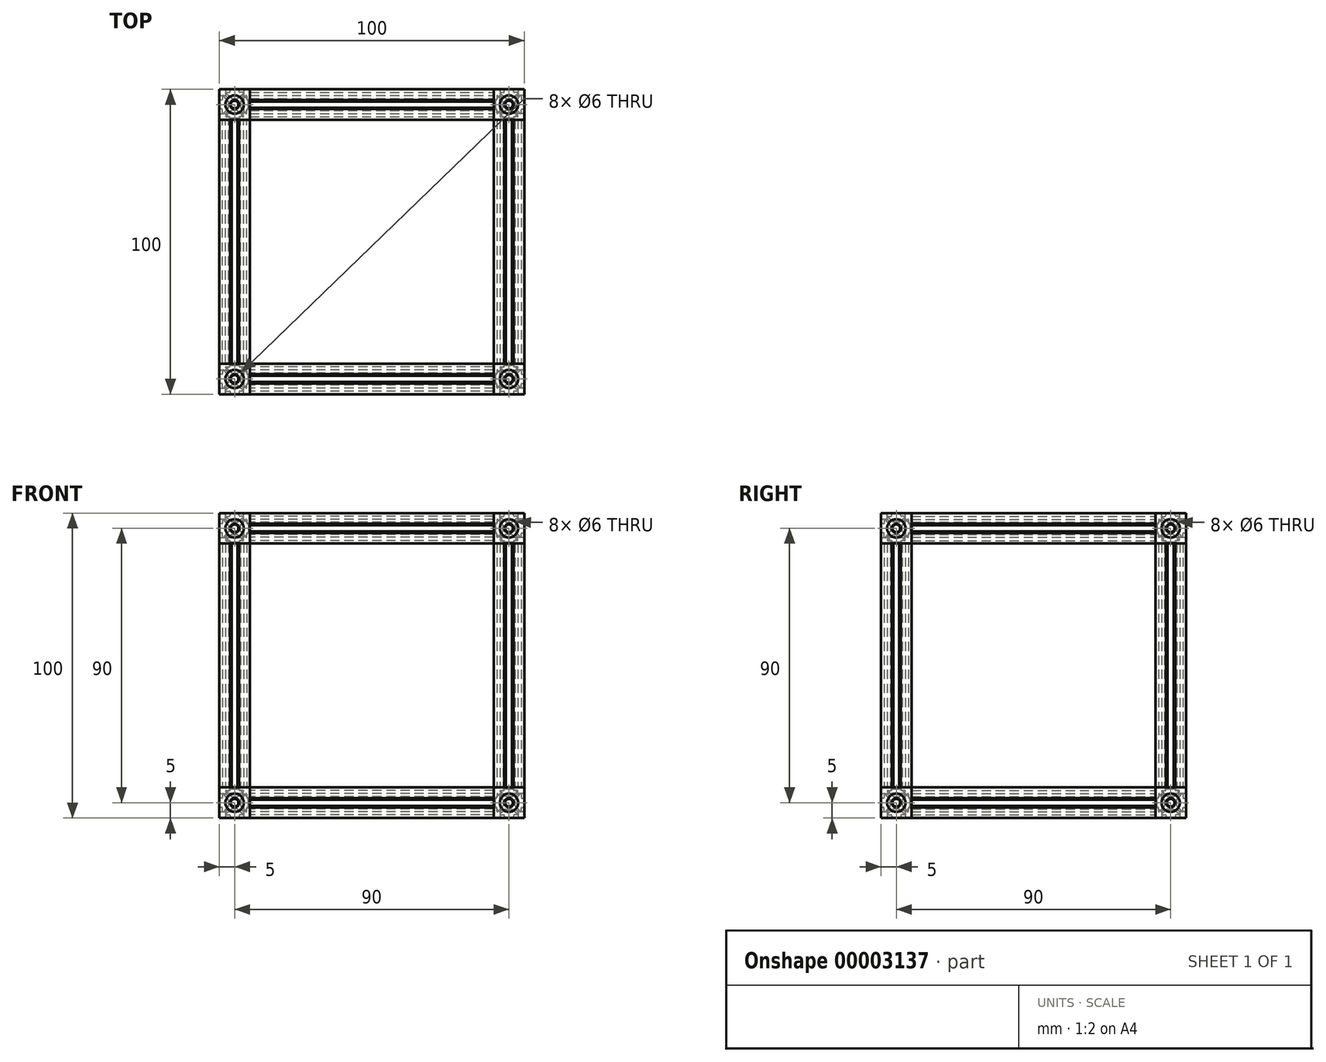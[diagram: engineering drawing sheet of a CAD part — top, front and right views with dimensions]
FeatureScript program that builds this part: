
annotation { "Feature Type Name" : "Feature", "Feature Type Description" : "" }
export const myFeature = defineFeature(function(context is Context, id is Id, definition is map)
    precondition{}
    {
        {
            var Q0;
            Q0=qCreatedBy(makeId("Front.planeOp"),FACE);
            var sketch = newSketch(context, id + "F0", { "sketchPlane" : qUnion([Q0])});
            skLineSegment(sketch, "E0", {"start": v(0, 0) * mm, "end": v(0, 5) * mm, "construction": true});
            skLineSegment(sketch, "E1", {"start": v(0, 0) * mm, "end": v(5, 5) * mm, "construction": true});
            skLineSegment(sketch, "E2", {"start": v(5, 5) * mm, "end": v(0, 5) * mm, "construction": true});
            skLineSegment(sketch, "E3", {"start": v(0, 2) * mm, "end": v(1, 2) * mm});
            skLineSegment(sketch, "E4", {"start": v(1, 2) * mm, "end": v(2.9, 3.65) * mm});
            skLineSegment(sketch, "E5", {"start": v(2.76, 4) * mm, "end": v(1.7, 4) * mm});
            skLineSegment(sketch, "E6", {"start": v(1.5, 4.2) * mm, "end": v(1.5, 4.8) * mm});
            skLineSegment(sketch, "E7", {"start": v(1.7, 5) * mm, "end": v(4.8, 5) * mm});
            skLineSegment(sketch, "E8.0.MirrorCS", {"start": v(5, 1.7) * mm, "end": v(5, 4.8) * mm});
            skLineSegment(sketch, "E8.1.MirrorCS", {"start": v(4.2, 1.5) * mm, "end": v(4.8, 1.5) * mm});
            skLineSegment(sketch, "E8.2.MirrorCS", {"start": v(4, 2.76) * mm, "end": v(4, 1.7) * mm});
            skLineSegment(sketch, "E8.3.MirrorCS", {"start": v(2, 0) * mm, "end": v(2, 1) * mm});
            skLineSegment(sketch, "E8.4.MirrorCS", {"start": v(2, 1) * mm, "end": v(3.65, 2.9) * mm});
            skLineSegment(sketch, "E9.0.MirrorCS", {"start": v(-2, 0) * mm, "end": v(-2, 1) * mm});
            skLineSegment(sketch, "E9.1.MirrorCS", {"start": v(-2, 1) * mm, "end": v(-3.65, 2.9) * mm});
            skLineSegment(sketch, "E9.2.MirrorCS", {"start": v(-4, 2.76) * mm, "end": v(-4, 1.7) * mm});
            skLineSegment(sketch, "E9.3.MirrorCS", {"start": v(-4.2, 1.5) * mm, "end": v(-4.8, 1.5) * mm});
            skLineSegment(sketch, "E9.4.MirrorCS", {"start": v(-5, 1.7) * mm, "end": v(-5, 4.8) * mm});
            skLineSegment(sketch, "E9.5.MirrorCS", {"start": v(-1.7, 5) * mm, "end": v(-4.8, 5) * mm});
            skLineSegment(sketch, "E9.6.MirrorCS", {"start": v(-1.5, 4.2) * mm, "end": v(-1.5, 4.8) * mm});
            skLineSegment(sketch, "E9.7.MirrorCS", {"start": v(-2.76, 4) * mm, "end": v(-1.7, 4) * mm});
            skLineSegment(sketch, "E9.8.MirrorCS", {"start": v(0, 2) * mm, "end": v(-1, 2) * mm});
            skLineSegment(sketch, "E9.9.MirrorCS", {"start": v(-1, 2) * mm, "end": v(-2.9, 3.65) * mm});
            skLineSegment(sketch, "E10.0.MirrorCS", {"start": v(0, 0) * mm, "end": v(5, 0) * mm, "construction": true});
            skLineSegment(sketch, "E11.0.MirrorCS", {"start": v(2, 0) * mm, "end": v(2, -1) * mm});
            skLineSegment(sketch, "E12.0.MirrorCS", {"start": v(2, -1) * mm, "end": v(3.65, -2.9) * mm});
            skLineSegment(sketch, "E13.0.MirrorCS", {"start": v(4.2, -1.5) * mm, "end": v(4.8, -1.5) * mm});
            skLineSegment(sketch, "E14.0.MirrorCS", {"start": v(5, -1.7) * mm, "end": v(5, -4.8) * mm});
            skLineSegment(sketch, "E15.0.MirrorCS", {"start": v(1.7, -5) * mm, "end": v(4.8, -5) * mm});
            skLineSegment(sketch, "E16.0.MirrorCS", {"start": v(1.5, -4.2) * mm, "end": v(1.5, -4.8) * mm});
            skLineSegment(sketch, "E17.0.MirrorCS", {"start": v(2.76, -4) * mm, "end": v(1.7, -4) * mm});
            skLineSegment(sketch, "E18.0.MirrorCS", {"start": v(1, -2) * mm, "end": v(2.9, -3.65) * mm});
            skLineSegment(sketch, "E19.0.MirrorCS", {"start": v(0, -2) * mm, "end": v(1, -2) * mm});
            skLineSegment(sketch, "E20.0.MirrorCS", {"start": v(0, -2) * mm, "end": v(-1, -2) * mm});
            skLineSegment(sketch, "E21.0.MirrorCS", {"start": v(-1, -2) * mm, "end": v(-2.9, -3.65) * mm});
            skLineSegment(sketch, "E22.0.MirrorCS", {"start": v(-2.76, -4) * mm, "end": v(-1.7, -4) * mm});
            skLineSegment(sketch, "E23.0.MirrorCS", {"start": v(-1.5, -4.2) * mm, "end": v(-1.5, -4.8) * mm});
            skLineSegment(sketch, "E24.0.MirrorCS", {"start": v(-1.7, -5) * mm, "end": v(-4.8, -5) * mm});
            skLineSegment(sketch, "E25.0.MirrorCS", {"start": v(-5, -1.7) * mm, "end": v(-5, -4.8) * mm});
            skLineSegment(sketch, "E26.0.MirrorCS", {"start": v(-4.2, -1.5) * mm, "end": v(-4.8, -1.5) * mm});
            skLineSegment(sketch, "E27.0.MirrorCS", {"start": v(-4, -2.76) * mm, "end": v(-4, -1.7) * mm});
            skLineSegment(sketch, "E28.0.MirrorCS", {"start": v(-2, -1) * mm, "end": v(-3.65, -2.9) * mm});
            skLineSegment(sketch, "E29.0.MirrorCS", {"start": v(-2, 0) * mm, "end": v(-2, -1) * mm});
            skLineSegment(sketch, "E30.0.MirrorCS", {"start": v(4, -2.76) * mm, "end": v(4, -1.7) * mm});
            skCircle(sketch, "E31", {"center": v(0, 0) * mm, "radius": 1.25 * mm});
            skPoint(sketch, "E32.visualSharp", {"position": v(-4, 3.3) * mm});
            skArc(sketch, "E32.filletArc", {"start": v(-3.65, 2.9) * mm, "mid": v(-3.87, 2.95) * mm, "end": v(-4, 2.76) * mm});
            skPoint(sketch, "E33.visualSharp", {"position": v(-5, 1.5) * mm});
            skArc(sketch, "E33.filletArc", {"start": v(-5, 1.7) * mm, "mid": v(-4.94, 1.56) * mm, "end": v(-4.8, 1.5) * mm});
            skPoint(sketch, "E34.visualSharp", {"position": v(-4, 1.5) * mm});
            skArc(sketch, "E34.filletArc", {"start": v(-4.2, 1.5) * mm, "mid": v(-4.06, 1.56) * mm, "end": v(-4, 1.7) * mm});
            skPoint(sketch, "E35.visualSharp", {"position": v(-5, 5) * mm});
            skArc(sketch, "E35.filletArc", {"start": v(-4.8, 5) * mm, "mid": v(-4.94, 4.94) * mm, "end": v(-5, 4.8) * mm});
            skPoint(sketch, "E36.visualSharp", {"position": v(-1.5, 5) * mm});
            skArc(sketch, "E36.filletArc", {"start": v(-1.5, 4.8) * mm, "mid": v(-1.56, 4.94) * mm, "end": v(-1.7, 5) * mm});
            skPoint(sketch, "E37.visualSharp", {"position": v(-1.5, 4) * mm});
            skArc(sketch, "E37.filletArc", {"start": v(-1.7, 4) * mm, "mid": v(-1.56, 4.06) * mm, "end": v(-1.5, 4.2) * mm});
            skPoint(sketch, "E38.visualSharp", {"position": v(-3.3, 4) * mm});
            skArc(sketch, "E38.filletArc", {"start": v(-2.76, 4) * mm, "mid": v(-2.95, 3.87) * mm, "end": v(-2.9, 3.65) * mm});
            skPoint(sketch, "E39.visualSharp", {"position": v(3.3, 4) * mm});
            skArc(sketch, "E39.filletArc", {"start": v(2.9, 3.65) * mm, "mid": v(2.95, 3.87) * mm, "end": v(2.76, 4) * mm});
            skPoint(sketch, "E40.visualSharp", {"position": v(1.5, 4) * mm});
            skArc(sketch, "E40.filletArc", {"start": v(1.5, 4.2) * mm, "mid": v(1.56, 4.06) * mm, "end": v(1.7, 4) * mm});
            skPoint(sketch, "E41.visualSharp", {"position": v(1.5, 5) * mm});
            skArc(sketch, "E41.filletArc", {"start": v(1.7, 5) * mm, "mid": v(1.56, 4.94) * mm, "end": v(1.5, 4.8) * mm});
            skPoint(sketch, "E42.visualSharp", {"position": v(5, 5) * mm});
            skArc(sketch, "E42.filletArc", {"start": v(5, 4.8) * mm, "mid": v(4.94, 4.94) * mm, "end": v(4.8, 5) * mm});
            skPoint(sketch, "E43.visualSharp", {"position": v(5, 1.5) * mm});
            skArc(sketch, "E43.filletArc", {"start": v(4.8, 1.5) * mm, "mid": v(4.94, 1.56) * mm, "end": v(5, 1.7) * mm});
            skPoint(sketch, "E44.visualSharp", {"position": v(4, 1.5) * mm});
            skArc(sketch, "E44.filletArc", {"start": v(4, 1.7) * mm, "mid": v(4.06, 1.56) * mm, "end": v(4.2, 1.5) * mm});
            skPoint(sketch, "E45.visualSharp", {"position": v(4, 3.3) * mm});
            skArc(sketch, "E45.filletArc", {"start": v(4, 2.76) * mm, "mid": v(3.87, 2.95) * mm, "end": v(3.65, 2.9) * mm});
            skPoint(sketch, "E46.visualSharp", {"position": v(4, -1.5) * mm});
            skArc(sketch, "E46.filletArc", {"start": v(4.2, -1.5) * mm, "mid": v(4.06, -1.56) * mm, "end": v(4, -1.7) * mm});
            skPoint(sketch, "E47.visualSharp", {"position": v(5, -1.5) * mm});
            skArc(sketch, "E47.filletArc", {"start": v(5, -1.7) * mm, "mid": v(4.94, -1.56) * mm, "end": v(4.8, -1.5) * mm});
            skPoint(sketch, "E48.visualSharp", {"position": v(4, -3.3) * mm});
            skArc(sketch, "E48.filletArc", {"start": v(3.65, -2.9) * mm, "mid": v(3.87, -2.95) * mm, "end": v(4, -2.76) * mm});
            skPoint(sketch, "E49.visualSharp", {"position": v(3.3, -4) * mm});
            skArc(sketch, "E49.filletArc", {"start": v(2.76, -4) * mm, "mid": v(2.95, -3.87) * mm, "end": v(2.9, -3.65) * mm});
            skPoint(sketch, "E50.visualSharp", {"position": v(5, -5) * mm});
            skArc(sketch, "E50.filletArc", {"start": v(4.8, -5) * mm, "mid": v(4.94, -4.94) * mm, "end": v(5, -4.8) * mm});
            skPoint(sketch, "E51.visualSharp", {"position": v(1.5, -5) * mm});
            skArc(sketch, "E51.filletArc", {"start": v(1.5, -4.8) * mm, "mid": v(1.56, -4.94) * mm, "end": v(1.7, -5) * mm});
            skPoint(sketch, "E52.visualSharp", {"position": v(1.5, -4) * mm});
            skArc(sketch, "E52.filletArc", {"start": v(1.7, -4) * mm, "mid": v(1.56, -4.06) * mm, "end": v(1.5, -4.2) * mm});
            skPoint(sketch, "E53.visualSharp", {"position": v(-1.5, -4) * mm});
            skArc(sketch, "E53.filletArc", {"start": v(-1.5, -4.2) * mm, "mid": v(-1.56, -4.06) * mm, "end": v(-1.7, -4) * mm});
            skPoint(sketch, "E54.visualSharp", {"position": v(-1.5, -5) * mm});
            skArc(sketch, "E54.filletArc", {"start": v(-1.7, -5) * mm, "mid": v(-1.56, -4.94) * mm, "end": v(-1.5, -4.8) * mm});
            skPoint(sketch, "E55.visualSharp", {"position": v(-3.3, -4) * mm});
            skArc(sketch, "E55.filletArc", {"start": v(-2.9, -3.65) * mm, "mid": v(-2.95, -3.87) * mm, "end": v(-2.76, -4) * mm});
            skPoint(sketch, "E56.visualSharp", {"position": v(-5, -5) * mm});
            skArc(sketch, "E56.filletArc", {"start": v(-5, -4.8) * mm, "mid": v(-4.94, -4.94) * mm, "end": v(-4.8, -5) * mm});
            skPoint(sketch, "E57.visualSharp", {"position": v(-4, -3.3) * mm});
            skArc(sketch, "E57.filletArc", {"start": v(-4, -2.76) * mm, "mid": v(-3.87, -2.95) * mm, "end": v(-3.65, -2.9) * mm});
            skPoint(sketch, "E58.visualSharp", {"position": v(-4, -1.5) * mm});
            skArc(sketch, "E58.filletArc", {"start": v(-4, -1.7) * mm, "mid": v(-4.06, -1.56) * mm, "end": v(-4.2, -1.5) * mm});
            skPoint(sketch, "E59.visualSharp", {"position": v(-5, -1.5) * mm});
            skArc(sketch, "E59.filletArc", {"start": v(-4.8, -1.5) * mm, "mid": v(-4.94, -1.56) * mm, "end": v(-5, -1.7) * mm});
            skSolve(sketch);
        }
        {
            var Q0;
            Q0=makeQuery(id+"F0.imprint","IMPRINT",FACE,{"disambiguationData":[TD([[makeQuery(id+"F0.imprint","IMPRINT",EDGE,{"derivedFrom":sQuery(id+"F0.wireOp",EDGE,"E3")}),-1.0]])]});
            extrude(context, id + "F1", {"entities" : qUnion([Q0]), "depth" : 80 * mm});
        }
        {
            var Q0;
            Q0=qCreatedBy(makeId("Front.planeOp"),FACE);
            var sketch = newSketch(context, id + "F2", { "sketchPlane" : qUnion([Q0])});
            skLineSegment(sketch, "E60.bottom", {"start": v(5, 5) * mm, "end": v(-5, 5) * mm});
            skLineSegment(sketch, "E60.left", {"start": v(5, 5) * mm, "end": v(5, -5) * mm});
            skLineSegment(sketch, "E61", {"start": v(5, -5) * mm, "end": v(-5, -5) * mm});
            skLineSegment(sketch, "E62", {"start": v(-5, -5) * mm, "end": v(-5, 5) * mm});
            skSolve(sketch);
        }
        {
            var Q0;
            Q0=makeQuery(id+"F2.imprint","IMPRINT",FACE,{"disambiguationData":[TD([[makeQuery(id+"F2.imprint","IMPRINT",EDGE,{"derivedFrom":sQuery(id+"F2.wireOp",EDGE,"E60.bottom")}),1.0]])]});
            extrude(context, id + "F3", {"entities" : qUnion([Q0]), "oppositeDirection" : true, "depth" : 10 * mm});
        }
        {
            var Q0;
            Q0=qCreatedBy(makeId("Top.planeOp"),FACE);
            var sketch = newSketch(context, id + "F4", { "sketchPlane" : qUnion([Q0])});
            skLineSegment(sketch, "E63", {"start": v(0, 0) * mm, "end": v(0, 10) * mm, "construction": true});
            skLineSegment(sketch, "E64", {"start": v(1.5, 0) * mm, "end": v(1.5, 0.5) * mm});
            skLineSegment(sketch, "E65", {"start": v(1.5, 0.5) * mm, "end": v(3, 2) * mm});
            skLineSegment(sketch, "E66", {"start": v(3, 2) * mm, "end": v(3, 10) * mm});
            skLineSegment(sketch, "E67", {"start": v(0, 10) * mm, "end": v(3, 10) * mm});
            skLineSegment(sketch, "E68", {"start": v(0, 0) * mm, "end": v(1.5, 0) * mm});
            skLineSegment(sketch, "E69", {"start": v(0, 10) * mm, "end": v(0, 0) * mm});
            skSolve(sketch);
        }
        {
            var Q0;
            Q0=makeQuery(id+"F4.imprint","IMPRINT",FACE,{"disambiguationData":[TD([[makeQuery(id+"F4.imprint","IMPRINT",EDGE,{"derivedFrom":sQuery(id+"F4.wireOp",EDGE,"E64")}),1.0]])]});
            var Q1;
            Q1=sQuery(id+"F4.wireOp",EDGE,"E69");
            revolve(context, id + "F5", {"operationType" : NewBodyOperationType.REMOVE, "entities" : qUnion([Q0]), "axis" : qUnion([Q1]), "revolveType" : RevolveType.FULL, "oppositeDirection" : true});
        }
        {
            var Q0;
            Q0=qCreatedBy(makeId("Top.planeOp"),FACE);
            var sketch = newSketch(context, id + "F6", { "sketchPlane" : qUnion([Q0])});
            skLineSegment(sketch, "E70", {"start": v(-5, 5) * mm, "end": v(5, 5) * mm, "construction": true});
            skLineSegment(sketch, "E71", {"start": v(-5, 5) * mm, "end": v(5, 5) * mm});
            skLineSegment(sketch, "E72", {"start": v(5, 5) * mm, "end": v(5, 6.5) * mm});
            skLineSegment(sketch, "E73", {"start": v(5, 6.5) * mm, "end": v(4.5, 6.5) * mm});
            skLineSegment(sketch, "E74", {"start": v(4.5, 6.5) * mm, "end": v(3, 8) * mm});
            skLineSegment(sketch, "E75", {"start": v(3, 8) * mm, "end": v(-5, 8) * mm});
            skLineSegment(sketch, "E76", {"start": v(-5, 8) * mm, "end": v(-5, 5) * mm});
            skSolve(sketch);
        }
        {
            var Q0;
            Q0=makeQuery(id+"F6.imprint","IMPRINT",FACE,{"disambiguationData":[TD([[makeQuery(id+"F6.imprint","IMPRINT",EDGE,{"derivedFrom":sQuery(id+"F6.wireOp",EDGE,"E71")}),1.0]])]});
            var Q1;
            Q1=sQuery(id+"F6.wireOp",EDGE,"E71");
            revolve(context, id + "F7", {"operationType" : NewBodyOperationType.REMOVE, "entities" : qUnion([Q0]), "axis" : qUnion([Q1]), "revolveType" : RevolveType.FULL, "oppositeDirection" : true});
        }
        {
            var Q0;
            Q0=qCreatedBy(makeId("Right.planeOp"),FACE);
            var sketch = newSketch(context, id + "F8", { "sketchPlane" : qUnion([Q0])});
            skLineSegment(sketch, "E77", {"start": v(5, 5) * mm, "end": v(5, -5) * mm, "construction": true});
            skLineSegment(sketch, "E78", {"start": v(5, 5) * mm, "end": v(6.5, 5) * mm});
            skLineSegment(sketch, "E79", {"start": v(6.5, 5) * mm, "end": v(6.5, 4.5) * mm});
            skLineSegment(sketch, "E80", {"start": v(6.5, 4.5) * mm, "end": v(8, 3) * mm});
            skLineSegment(sketch, "E81", {"start": v(8, 3) * mm, "end": v(8, -5) * mm});
            skLineSegment(sketch, "E82", {"start": v(8, -5) * mm, "end": v(5, -5) * mm});
            skLineSegment(sketch, "E83", {"start": v(5, -5) * mm, "end": v(5, 5) * mm});
            skSolve(sketch);
        }
        {
            var Q0;
            Q0=makeQuery(id+"F8.imprint","IMPRINT",FACE,{"disambiguationData":[TD([[makeQuery(id+"F8.imprint","IMPRINT",EDGE,{"derivedFrom":sQuery(id+"F8.wireOp",EDGE,"E78")}),-1.0]])]});
            var Q1;
            Q1=sQuery(id+"F8.wireOp",EDGE,"E83");
            revolve(context, id + "F9", {"operationType" : NewBodyOperationType.REMOVE, "entities" : qUnion([Q0]), "axis" : qUnion([Q1]), "revolveType" : RevolveType.FULL});
        }
        {
            var Q0;
            Q0=makeQuery(id+"F1.opExtrude","SWEPT_BODY",BODY,{"disambiguationData":[OSD([sQuery(id+"F0.wireOp",EDGE,"E3"),sQuery(id+"F0.wireOp",EDGE,"E4"),sQuery(id+"F0.wireOp",EDGE,"E5"),sQuery(id+"F0.wireOp",EDGE,"E6"),sQuery(id+"F0.wireOp",EDGE,"E7"),sQuery(id+"F0.wireOp",EDGE,"E8.0.MirrorCS"),sQuery(id+"F0.wireOp",EDGE,"E8.1.MirrorCS"),sQuery(id+"F0.wireOp",EDGE,"E8.2.MirrorCS"),sQuery(id+"F0.wireOp",EDGE,"E8.4.MirrorCS"),sQuery(id+"F0.wireOp",EDGE,"E9.0.MirrorCS"),sQuery(id+"F0.wireOp",EDGE,"E9.1.MirrorCS"),sQuery(id+"F0.wireOp",EDGE,"E9.2.MirrorCS"),sQuery(id+"F0.wireOp",EDGE,"E9.3.MirrorCS"),sQuery(id+"F0.wireOp",EDGE,"E9.4.MirrorCS"),sQuery(id+"F0.wireOp",EDGE,"E9.5.MirrorCS"),sQuery(id+"F0.wireOp",EDGE,"E9.6.MirrorCS"),sQuery(id+"F0.wireOp",EDGE,"E9.7.MirrorCS"),sQuery(id+"F0.wireOp",EDGE,"E9.9.MirrorCS"),sQuery(id+"F0.wireOp",EDGE,"E11.0.MirrorCS"),sQuery(id+"F0.wireOp",EDGE,"E12.0.MirrorCS"),sQuery(id+"F0.wireOp",EDGE,"E13.0.MirrorCS"),sQuery(id+"F0.wireOp",EDGE,"E14.0.MirrorCS"),sQuery(id+"F0.wireOp",EDGE,"E15.0.MirrorCS"),sQuery(id+"F0.wireOp",EDGE,"E16.0.MirrorCS"),sQuery(id+"F0.wireOp",EDGE,"E17.0.MirrorCS"),sQuery(id+"F0.wireOp",EDGE,"E18.0.MirrorCS"),sQuery(id+"F0.wireOp",EDGE,"E20.0.MirrorCS"),sQuery(id+"F0.wireOp",EDGE,"E21.0.MirrorCS"),sQuery(id+"F0.wireOp",EDGE,"E22.0.MirrorCS"),sQuery(id+"F0.wireOp",EDGE,"E23.0.MirrorCS"),sQuery(id+"F0.wireOp",EDGE,"E24.0.MirrorCS"),sQuery(id+"F0.wireOp",EDGE,"E25.0.MirrorCS"),sQuery(id+"F0.wireOp",EDGE,"E26.0.MirrorCS"),sQuery(id+"F0.wireOp",EDGE,"E27.0.MirrorCS"),sQuery(id+"F0.wireOp",EDGE,"E28.0.MirrorCS"),sQuery(id+"F0.wireOp",EDGE,"E30.0.MirrorCS"),sQuery(id+"F0.wireOp",EDGE,"E31"),sQuery(id+"F0.wireOp",EDGE,"E32.filletArc"),sQuery(id+"F0.wireOp",EDGE,"E33.filletArc"),sQuery(id+"F0.wireOp",EDGE,"E34.filletArc"),sQuery(id+"F0.wireOp",EDGE,"E35.filletArc"),sQuery(id+"F0.wireOp",EDGE,"E36.filletArc"),sQuery(id+"F0.wireOp",EDGE,"E37.filletArc"),sQuery(id+"F0.wireOp",EDGE,"E38.filletArc"),sQuery(id+"F0.wireOp",EDGE,"E39.filletArc"),sQuery(id+"F0.wireOp",EDGE,"E40.filletArc"),sQuery(id+"F0.wireOp",EDGE,"E41.filletArc"),sQuery(id+"F0.wireOp",EDGE,"E42.filletArc"),sQuery(id+"F0.wireOp",EDGE,"E43.filletArc"),sQuery(id+"F0.wireOp",EDGE,"E44.filletArc"),sQuery(id+"F0.wireOp",EDGE,"E45.filletArc"),sQuery(id+"F0.wireOp",EDGE,"E46.filletArc"),sQuery(id+"F0.wireOp",EDGE,"E47.filletArc"),sQuery(id+"F0.wireOp",EDGE,"E48.filletArc"),sQuery(id+"F0.wireOp",EDGE,"E49.filletArc"),sQuery(id+"F0.wireOp",EDGE,"E50.filletArc"),sQuery(id+"F0.wireOp",EDGE,"E51.filletArc"),sQuery(id+"F0.wireOp",EDGE,"E52.filletArc"),sQuery(id+"F0.wireOp",EDGE,"E53.filletArc"),sQuery(id+"F0.wireOp",EDGE,"E54.filletArc"),sQuery(id+"F0.wireOp",EDGE,"E55.filletArc"),sQuery(id+"F0.wireOp",EDGE,"E56.filletArc"),sQuery(id+"F0.wireOp",EDGE,"E57.filletArc"),sQuery(id+"F0.wireOp",EDGE,"E58.filletArc"),sQuery(id+"F0.wireOp",EDGE,"E59.filletArc")])]});
            var Q1;
            Q1=sQuery(id+"F6.wireOp",EDGE,"E71");
            circularPattern(context, id + "F10", {"entities" : qUnion([Q0]), "axis" : qUnion([Q1]), "angle" : 90 * degree, "instanceCount" : 2, "oppositeDirection" : true});
        }
        {
            var Q0;
            Q0=qCreatedBy(makeId("Right.planeOp"),FACE);
            cPlane(context, id + "F11", {"entities" : qUnion([Q0]), "cplaneType" : CPlaneType.OFFSET, "offset" : 45 * mm, "width" : 150 * mm, "height" : 150 * mm});
        }
        {
            var Q0;
            Q0=qCreatedBy(id+"F11.planeOp",FACE);
            var sketch = newSketch(context, id + "F12", { "sketchPlane" : qUnion([Q0])});
            skLineSegment(sketch, "E84", {"start": v(-40, 5) * mm, "end": v(-40, -5) * mm, "construction": true});
            skSolve(sketch);
        }
        {
            var Q0;
            Q0=makeQuery(id+"F3.opExtrude","SWEPT_BODY",BODY,{"disambiguationData":[OSD([sQuery(id+"F2.wireOp",EDGE,"E60.bottom"),sQuery(id+"F2.wireOp",EDGE,"E60.left"),sQuery(id+"F2.wireOp",EDGE,"E61"),sQuery(id+"F2.wireOp",EDGE,"E62")])]});
            var Q1;
            Q1=makeQuery(id+"F1.opExtrude","SWEPT_BODY",BODY,{"disambiguationData":[OSD([sQuery(id+"F0.wireOp",EDGE,"E3"),sQuery(id+"F0.wireOp",EDGE,"E4"),sQuery(id+"F0.wireOp",EDGE,"E5"),sQuery(id+"F0.wireOp",EDGE,"E6"),sQuery(id+"F0.wireOp",EDGE,"E7"),sQuery(id+"F0.wireOp",EDGE,"E8.0.MirrorCS"),sQuery(id+"F0.wireOp",EDGE,"E8.1.MirrorCS"),sQuery(id+"F0.wireOp",EDGE,"E8.2.MirrorCS"),sQuery(id+"F0.wireOp",EDGE,"E8.4.MirrorCS"),sQuery(id+"F0.wireOp",EDGE,"E9.0.MirrorCS"),sQuery(id+"F0.wireOp",EDGE,"E9.1.MirrorCS"),sQuery(id+"F0.wireOp",EDGE,"E9.2.MirrorCS"),sQuery(id+"F0.wireOp",EDGE,"E9.3.MirrorCS"),sQuery(id+"F0.wireOp",EDGE,"E9.4.MirrorCS"),sQuery(id+"F0.wireOp",EDGE,"E9.5.MirrorCS"),sQuery(id+"F0.wireOp",EDGE,"E9.6.MirrorCS"),sQuery(id+"F0.wireOp",EDGE,"E9.7.MirrorCS"),sQuery(id+"F0.wireOp",EDGE,"E9.9.MirrorCS"),sQuery(id+"F0.wireOp",EDGE,"E11.0.MirrorCS"),sQuery(id+"F0.wireOp",EDGE,"E12.0.MirrorCS"),sQuery(id+"F0.wireOp",EDGE,"E13.0.MirrorCS"),sQuery(id+"F0.wireOp",EDGE,"E14.0.MirrorCS"),sQuery(id+"F0.wireOp",EDGE,"E15.0.MirrorCS"),sQuery(id+"F0.wireOp",EDGE,"E16.0.MirrorCS"),sQuery(id+"F0.wireOp",EDGE,"E17.0.MirrorCS"),sQuery(id+"F0.wireOp",EDGE,"E18.0.MirrorCS"),sQuery(id+"F0.wireOp",EDGE,"E20.0.MirrorCS"),sQuery(id+"F0.wireOp",EDGE,"E21.0.MirrorCS"),sQuery(id+"F0.wireOp",EDGE,"E22.0.MirrorCS"),sQuery(id+"F0.wireOp",EDGE,"E23.0.MirrorCS"),sQuery(id+"F0.wireOp",EDGE,"E24.0.MirrorCS"),sQuery(id+"F0.wireOp",EDGE,"E25.0.MirrorCS"),sQuery(id+"F0.wireOp",EDGE,"E26.0.MirrorCS"),sQuery(id+"F0.wireOp",EDGE,"E27.0.MirrorCS"),sQuery(id+"F0.wireOp",EDGE,"E28.0.MirrorCS"),sQuery(id+"F0.wireOp",EDGE,"E30.0.MirrorCS"),sQuery(id+"F0.wireOp",EDGE,"E31"),sQuery(id+"F0.wireOp",EDGE,"E32.filletArc"),sQuery(id+"F0.wireOp",EDGE,"E33.filletArc"),sQuery(id+"F0.wireOp",EDGE,"E34.filletArc"),sQuery(id+"F0.wireOp",EDGE,"E35.filletArc"),sQuery(id+"F0.wireOp",EDGE,"E36.filletArc"),sQuery(id+"F0.wireOp",EDGE,"E37.filletArc"),sQuery(id+"F0.wireOp",EDGE,"E38.filletArc"),sQuery(id+"F0.wireOp",EDGE,"E39.filletArc"),sQuery(id+"F0.wireOp",EDGE,"E40.filletArc"),sQuery(id+"F0.wireOp",EDGE,"E41.filletArc"),sQuery(id+"F0.wireOp",EDGE,"E42.filletArc"),sQuery(id+"F0.wireOp",EDGE,"E43.filletArc"),sQuery(id+"F0.wireOp",EDGE,"E44.filletArc"),sQuery(id+"F0.wireOp",EDGE,"E45.filletArc"),sQuery(id+"F0.wireOp",EDGE,"E46.filletArc"),sQuery(id+"F0.wireOp",EDGE,"E47.filletArc"),sQuery(id+"F0.wireOp",EDGE,"E48.filletArc"),sQuery(id+"F0.wireOp",EDGE,"E49.filletArc"),sQuery(id+"F0.wireOp",EDGE,"E50.filletArc"),sQuery(id+"F0.wireOp",EDGE,"E51.filletArc"),sQuery(id+"F0.wireOp",EDGE,"E52.filletArc"),sQuery(id+"F0.wireOp",EDGE,"E53.filletArc"),sQuery(id+"F0.wireOp",EDGE,"E54.filletArc"),sQuery(id+"F0.wireOp",EDGE,"E55.filletArc"),sQuery(id+"F0.wireOp",EDGE,"E56.filletArc"),sQuery(id+"F0.wireOp",EDGE,"E57.filletArc"),sQuery(id+"F0.wireOp",EDGE,"E58.filletArc"),sQuery(id+"F0.wireOp",EDGE,"E59.filletArc")])]});
            var Q2;
            Q2=makeQuery(id+"F10.opPattern","COPY",BODY,{"derivedFrom":makeQuery(id+"F1.opExtrude","SWEPT_BODY",BODY,{"disambiguationData":[OSD([sQuery(id+"F0.wireOp",EDGE,"E3"),sQuery(id+"F0.wireOp",EDGE,"E4"),sQuery(id+"F0.wireOp",EDGE,"E5"),sQuery(id+"F0.wireOp",EDGE,"E6"),sQuery(id+"F0.wireOp",EDGE,"E7"),sQuery(id+"F0.wireOp",EDGE,"E8.0.MirrorCS"),sQuery(id+"F0.wireOp",EDGE,"E8.1.MirrorCS"),sQuery(id+"F0.wireOp",EDGE,"E8.2.MirrorCS"),sQuery(id+"F0.wireOp",EDGE,"E8.4.MirrorCS"),sQuery(id+"F0.wireOp",EDGE,"E9.0.MirrorCS"),sQuery(id+"F0.wireOp",EDGE,"E9.1.MirrorCS"),sQuery(id+"F0.wireOp",EDGE,"E9.2.MirrorCS"),sQuery(id+"F0.wireOp",EDGE,"E9.3.MirrorCS"),sQuery(id+"F0.wireOp",EDGE,"E9.4.MirrorCS"),sQuery(id+"F0.wireOp",EDGE,"E9.5.MirrorCS"),sQuery(id+"F0.wireOp",EDGE,"E9.6.MirrorCS"),sQuery(id+"F0.wireOp",EDGE,"E9.7.MirrorCS"),sQuery(id+"F0.wireOp",EDGE,"E9.9.MirrorCS"),sQuery(id+"F0.wireOp",EDGE,"E11.0.MirrorCS"),sQuery(id+"F0.wireOp",EDGE,"E12.0.MirrorCS"),sQuery(id+"F0.wireOp",EDGE,"E13.0.MirrorCS"),sQuery(id+"F0.wireOp",EDGE,"E14.0.MirrorCS"),sQuery(id+"F0.wireOp",EDGE,"E15.0.MirrorCS"),sQuery(id+"F0.wireOp",EDGE,"E16.0.MirrorCS"),sQuery(id+"F0.wireOp",EDGE,"E17.0.MirrorCS"),sQuery(id+"F0.wireOp",EDGE,"E18.0.MirrorCS"),sQuery(id+"F0.wireOp",EDGE,"E20.0.MirrorCS"),sQuery(id+"F0.wireOp",EDGE,"E21.0.MirrorCS"),sQuery(id+"F0.wireOp",EDGE,"E22.0.MirrorCS"),sQuery(id+"F0.wireOp",EDGE,"E23.0.MirrorCS"),sQuery(id+"F0.wireOp",EDGE,"E24.0.MirrorCS"),sQuery(id+"F0.wireOp",EDGE,"E25.0.MirrorCS"),sQuery(id+"F0.wireOp",EDGE,"E26.0.MirrorCS"),sQuery(id+"F0.wireOp",EDGE,"E27.0.MirrorCS"),sQuery(id+"F0.wireOp",EDGE,"E28.0.MirrorCS"),sQuery(id+"F0.wireOp",EDGE,"E30.0.MirrorCS"),sQuery(id+"F0.wireOp",EDGE,"E31"),sQuery(id+"F0.wireOp",EDGE,"E32.filletArc"),sQuery(id+"F0.wireOp",EDGE,"E33.filletArc"),sQuery(id+"F0.wireOp",EDGE,"E34.filletArc"),sQuery(id+"F0.wireOp",EDGE,"E35.filletArc"),sQuery(id+"F0.wireOp",EDGE,"E36.filletArc"),sQuery(id+"F0.wireOp",EDGE,"E37.filletArc"),sQuery(id+"F0.wireOp",EDGE,"E38.filletArc"),sQuery(id+"F0.wireOp",EDGE,"E39.filletArc"),sQuery(id+"F0.wireOp",EDGE,"E40.filletArc"),sQuery(id+"F0.wireOp",EDGE,"E41.filletArc"),sQuery(id+"F0.wireOp",EDGE,"E42.filletArc"),sQuery(id+"F0.wireOp",EDGE,"E43.filletArc"),sQuery(id+"F0.wireOp",EDGE,"E44.filletArc"),sQuery(id+"F0.wireOp",EDGE,"E45.filletArc"),sQuery(id+"F0.wireOp",EDGE,"E46.filletArc"),sQuery(id+"F0.wireOp",EDGE,"E47.filletArc"),sQuery(id+"F0.wireOp",EDGE,"E48.filletArc"),sQuery(id+"F0.wireOp",EDGE,"E49.filletArc"),sQuery(id+"F0.wireOp",EDGE,"E50.filletArc"),sQuery(id+"F0.wireOp",EDGE,"E51.filletArc"),sQuery(id+"F0.wireOp",EDGE,"E52.filletArc"),sQuery(id+"F0.wireOp",EDGE,"E53.filletArc"),sQuery(id+"F0.wireOp",EDGE,"E54.filletArc"),sQuery(id+"F0.wireOp",EDGE,"E55.filletArc"),sQuery(id+"F0.wireOp",EDGE,"E56.filletArc"),sQuery(id+"F0.wireOp",EDGE,"E57.filletArc"),sQuery(id+"F0.wireOp",EDGE,"E58.filletArc"),sQuery(id+"F0.wireOp",EDGE,"E59.filletArc")])]}),"instanceName":"1"});
            var Q3;
            Q3=sQuery(id+"F12.wireOp",EDGE,"E84");
            circularPattern(context, id + "F13", {"entities" : qUnion([Q0, Q1, Q2]), "axis" : qUnion([Q3]), "angle" : 90 * degree, "instanceCount" : 4});
        }
        {
            var Q0;
            Q0=qCreatedBy(makeId("Top.planeOp"),FACE);
            cPlane(context, id + "F14", {"entities" : qUnion([Q0]), "cplaneType" : CPlaneType.OFFSET, "offset" : 45 * mm, "width" : 150 * mm, "height" : 150 * mm});
        }
        {
            var Q0;
            Q0=makeQuery(id+"F13.opPattern","COPY",BODY,{"derivedFrom":makeQuery(id+"F3.opExtrude","SWEPT_BODY",BODY,{"disambiguationData":[OSD([sQuery(id+"F2.wireOp",EDGE,"E60.bottom"),sQuery(id+"F2.wireOp",EDGE,"E60.left"),sQuery(id+"F2.wireOp",EDGE,"E61"),sQuery(id+"F2.wireOp",EDGE,"E62")])]}),"instanceName":"3"});
            var Q1;
            Q1=makeQuery(id+"F1.opExtrude","SWEPT_BODY",BODY,{"disambiguationData":[OSD([sQuery(id+"F0.wireOp",EDGE,"E3"),sQuery(id+"F0.wireOp",EDGE,"E4"),sQuery(id+"F0.wireOp",EDGE,"E5"),sQuery(id+"F0.wireOp",EDGE,"E6"),sQuery(id+"F0.wireOp",EDGE,"E7"),sQuery(id+"F0.wireOp",EDGE,"E8.0.MirrorCS"),sQuery(id+"F0.wireOp",EDGE,"E8.1.MirrorCS"),sQuery(id+"F0.wireOp",EDGE,"E8.2.MirrorCS"),sQuery(id+"F0.wireOp",EDGE,"E8.4.MirrorCS"),sQuery(id+"F0.wireOp",EDGE,"E9.0.MirrorCS"),sQuery(id+"F0.wireOp",EDGE,"E9.1.MirrorCS"),sQuery(id+"F0.wireOp",EDGE,"E9.2.MirrorCS"),sQuery(id+"F0.wireOp",EDGE,"E9.3.MirrorCS"),sQuery(id+"F0.wireOp",EDGE,"E9.4.MirrorCS"),sQuery(id+"F0.wireOp",EDGE,"E9.5.MirrorCS"),sQuery(id+"F0.wireOp",EDGE,"E9.6.MirrorCS"),sQuery(id+"F0.wireOp",EDGE,"E9.7.MirrorCS"),sQuery(id+"F0.wireOp",EDGE,"E9.9.MirrorCS"),sQuery(id+"F0.wireOp",EDGE,"E11.0.MirrorCS"),sQuery(id+"F0.wireOp",EDGE,"E12.0.MirrorCS"),sQuery(id+"F0.wireOp",EDGE,"E13.0.MirrorCS"),sQuery(id+"F0.wireOp",EDGE,"E14.0.MirrorCS"),sQuery(id+"F0.wireOp",EDGE,"E15.0.MirrorCS"),sQuery(id+"F0.wireOp",EDGE,"E16.0.MirrorCS"),sQuery(id+"F0.wireOp",EDGE,"E17.0.MirrorCS"),sQuery(id+"F0.wireOp",EDGE,"E18.0.MirrorCS"),sQuery(id+"F0.wireOp",EDGE,"E20.0.MirrorCS"),sQuery(id+"F0.wireOp",EDGE,"E21.0.MirrorCS"),sQuery(id+"F0.wireOp",EDGE,"E22.0.MirrorCS"),sQuery(id+"F0.wireOp",EDGE,"E23.0.MirrorCS"),sQuery(id+"F0.wireOp",EDGE,"E24.0.MirrorCS"),sQuery(id+"F0.wireOp",EDGE,"E25.0.MirrorCS"),sQuery(id+"F0.wireOp",EDGE,"E26.0.MirrorCS"),sQuery(id+"F0.wireOp",EDGE,"E27.0.MirrorCS"),sQuery(id+"F0.wireOp",EDGE,"E28.0.MirrorCS"),sQuery(id+"F0.wireOp",EDGE,"E30.0.MirrorCS"),sQuery(id+"F0.wireOp",EDGE,"E31"),sQuery(id+"F0.wireOp",EDGE,"E32.filletArc"),sQuery(id+"F0.wireOp",EDGE,"E33.filletArc"),sQuery(id+"F0.wireOp",EDGE,"E34.filletArc"),sQuery(id+"F0.wireOp",EDGE,"E35.filletArc"),sQuery(id+"F0.wireOp",EDGE,"E36.filletArc"),sQuery(id+"F0.wireOp",EDGE,"E37.filletArc"),sQuery(id+"F0.wireOp",EDGE,"E38.filletArc"),sQuery(id+"F0.wireOp",EDGE,"E39.filletArc"),sQuery(id+"F0.wireOp",EDGE,"E40.filletArc"),sQuery(id+"F0.wireOp",EDGE,"E41.filletArc"),sQuery(id+"F0.wireOp",EDGE,"E42.filletArc"),sQuery(id+"F0.wireOp",EDGE,"E43.filletArc"),sQuery(id+"F0.wireOp",EDGE,"E44.filletArc"),sQuery(id+"F0.wireOp",EDGE,"E45.filletArc"),sQuery(id+"F0.wireOp",EDGE,"E46.filletArc"),sQuery(id+"F0.wireOp",EDGE,"E47.filletArc"),sQuery(id+"F0.wireOp",EDGE,"E48.filletArc"),sQuery(id+"F0.wireOp",EDGE,"E49.filletArc"),sQuery(id+"F0.wireOp",EDGE,"E50.filletArc"),sQuery(id+"F0.wireOp",EDGE,"E51.filletArc"),sQuery(id+"F0.wireOp",EDGE,"E52.filletArc"),sQuery(id+"F0.wireOp",EDGE,"E53.filletArc"),sQuery(id+"F0.wireOp",EDGE,"E54.filletArc"),sQuery(id+"F0.wireOp",EDGE,"E55.filletArc"),sQuery(id+"F0.wireOp",EDGE,"E56.filletArc"),sQuery(id+"F0.wireOp",EDGE,"E57.filletArc"),sQuery(id+"F0.wireOp",EDGE,"E58.filletArc"),sQuery(id+"F0.wireOp",EDGE,"E59.filletArc")])]});
            var Q2;
            Q2=makeQuery(id+"F13.opPattern","COPY",BODY,{"derivedFrom":makeQuery(id+"F1.opExtrude","SWEPT_BODY",BODY,{"disambiguationData":[OSD([sQuery(id+"F0.wireOp",EDGE,"E3"),sQuery(id+"F0.wireOp",EDGE,"E4"),sQuery(id+"F0.wireOp",EDGE,"E5"),sQuery(id+"F0.wireOp",EDGE,"E6"),sQuery(id+"F0.wireOp",EDGE,"E7"),sQuery(id+"F0.wireOp",EDGE,"E8.0.MirrorCS"),sQuery(id+"F0.wireOp",EDGE,"E8.1.MirrorCS"),sQuery(id+"F0.wireOp",EDGE,"E8.2.MirrorCS"),sQuery(id+"F0.wireOp",EDGE,"E8.4.MirrorCS"),sQuery(id+"F0.wireOp",EDGE,"E9.0.MirrorCS"),sQuery(id+"F0.wireOp",EDGE,"E9.1.MirrorCS"),sQuery(id+"F0.wireOp",EDGE,"E9.2.MirrorCS"),sQuery(id+"F0.wireOp",EDGE,"E9.3.MirrorCS"),sQuery(id+"F0.wireOp",EDGE,"E9.4.MirrorCS"),sQuery(id+"F0.wireOp",EDGE,"E9.5.MirrorCS"),sQuery(id+"F0.wireOp",EDGE,"E9.6.MirrorCS"),sQuery(id+"F0.wireOp",EDGE,"E9.7.MirrorCS"),sQuery(id+"F0.wireOp",EDGE,"E9.9.MirrorCS"),sQuery(id+"F0.wireOp",EDGE,"E11.0.MirrorCS"),sQuery(id+"F0.wireOp",EDGE,"E12.0.MirrorCS"),sQuery(id+"F0.wireOp",EDGE,"E13.0.MirrorCS"),sQuery(id+"F0.wireOp",EDGE,"E14.0.MirrorCS"),sQuery(id+"F0.wireOp",EDGE,"E15.0.MirrorCS"),sQuery(id+"F0.wireOp",EDGE,"E16.0.MirrorCS"),sQuery(id+"F0.wireOp",EDGE,"E17.0.MirrorCS"),sQuery(id+"F0.wireOp",EDGE,"E18.0.MirrorCS"),sQuery(id+"F0.wireOp",EDGE,"E20.0.MirrorCS"),sQuery(id+"F0.wireOp",EDGE,"E21.0.MirrorCS"),sQuery(id+"F0.wireOp",EDGE,"E22.0.MirrorCS"),sQuery(id+"F0.wireOp",EDGE,"E23.0.MirrorCS"),sQuery(id+"F0.wireOp",EDGE,"E24.0.MirrorCS"),sQuery(id+"F0.wireOp",EDGE,"E25.0.MirrorCS"),sQuery(id+"F0.wireOp",EDGE,"E26.0.MirrorCS"),sQuery(id+"F0.wireOp",EDGE,"E27.0.MirrorCS"),sQuery(id+"F0.wireOp",EDGE,"E28.0.MirrorCS"),sQuery(id+"F0.wireOp",EDGE,"E30.0.MirrorCS"),sQuery(id+"F0.wireOp",EDGE,"E31"),sQuery(id+"F0.wireOp",EDGE,"E32.filletArc"),sQuery(id+"F0.wireOp",EDGE,"E33.filletArc"),sQuery(id+"F0.wireOp",EDGE,"E34.filletArc"),sQuery(id+"F0.wireOp",EDGE,"E35.filletArc"),sQuery(id+"F0.wireOp",EDGE,"E36.filletArc"),sQuery(id+"F0.wireOp",EDGE,"E37.filletArc"),sQuery(id+"F0.wireOp",EDGE,"E38.filletArc"),sQuery(id+"F0.wireOp",EDGE,"E39.filletArc"),sQuery(id+"F0.wireOp",EDGE,"E40.filletArc"),sQuery(id+"F0.wireOp",EDGE,"E41.filletArc"),sQuery(id+"F0.wireOp",EDGE,"E42.filletArc"),sQuery(id+"F0.wireOp",EDGE,"E43.filletArc"),sQuery(id+"F0.wireOp",EDGE,"E44.filletArc"),sQuery(id+"F0.wireOp",EDGE,"E45.filletArc"),sQuery(id+"F0.wireOp",EDGE,"E46.filletArc"),sQuery(id+"F0.wireOp",EDGE,"E47.filletArc"),sQuery(id+"F0.wireOp",EDGE,"E48.filletArc"),sQuery(id+"F0.wireOp",EDGE,"E49.filletArc"),sQuery(id+"F0.wireOp",EDGE,"E50.filletArc"),sQuery(id+"F0.wireOp",EDGE,"E51.filletArc"),sQuery(id+"F0.wireOp",EDGE,"E52.filletArc"),sQuery(id+"F0.wireOp",EDGE,"E53.filletArc"),sQuery(id+"F0.wireOp",EDGE,"E54.filletArc"),sQuery(id+"F0.wireOp",EDGE,"E55.filletArc"),sQuery(id+"F0.wireOp",EDGE,"E56.filletArc"),sQuery(id+"F0.wireOp",EDGE,"E57.filletArc"),sQuery(id+"F0.wireOp",EDGE,"E58.filletArc"),sQuery(id+"F0.wireOp",EDGE,"E59.filletArc")])]}),"instanceName":"3"});
            var Q3;
            Q3=makeQuery(id+"F13.opPattern","COPY",BODY,{"derivedFrom":makeQuery(id+"F3.opExtrude","SWEPT_BODY",BODY,{"disambiguationData":[OSD([sQuery(id+"F2.wireOp",EDGE,"E60.bottom"),sQuery(id+"F2.wireOp",EDGE,"E60.left"),sQuery(id+"F2.wireOp",EDGE,"E61"),sQuery(id+"F2.wireOp",EDGE,"E62")])]}),"instanceName":"2"});
            var Q4;
            Q4=makeQuery(id+"F13.opPattern","COPY",BODY,{"derivedFrom":makeQuery(id+"F1.opExtrude","SWEPT_BODY",BODY,{"disambiguationData":[OSD([sQuery(id+"F0.wireOp",EDGE,"E3"),sQuery(id+"F0.wireOp",EDGE,"E4"),sQuery(id+"F0.wireOp",EDGE,"E5"),sQuery(id+"F0.wireOp",EDGE,"E6"),sQuery(id+"F0.wireOp",EDGE,"E7"),sQuery(id+"F0.wireOp",EDGE,"E8.0.MirrorCS"),sQuery(id+"F0.wireOp",EDGE,"E8.1.MirrorCS"),sQuery(id+"F0.wireOp",EDGE,"E8.2.MirrorCS"),sQuery(id+"F0.wireOp",EDGE,"E8.4.MirrorCS"),sQuery(id+"F0.wireOp",EDGE,"E9.0.MirrorCS"),sQuery(id+"F0.wireOp",EDGE,"E9.1.MirrorCS"),sQuery(id+"F0.wireOp",EDGE,"E9.2.MirrorCS"),sQuery(id+"F0.wireOp",EDGE,"E9.3.MirrorCS"),sQuery(id+"F0.wireOp",EDGE,"E9.4.MirrorCS"),sQuery(id+"F0.wireOp",EDGE,"E9.5.MirrorCS"),sQuery(id+"F0.wireOp",EDGE,"E9.6.MirrorCS"),sQuery(id+"F0.wireOp",EDGE,"E9.7.MirrorCS"),sQuery(id+"F0.wireOp",EDGE,"E9.9.MirrorCS"),sQuery(id+"F0.wireOp",EDGE,"E11.0.MirrorCS"),sQuery(id+"F0.wireOp",EDGE,"E12.0.MirrorCS"),sQuery(id+"F0.wireOp",EDGE,"E13.0.MirrorCS"),sQuery(id+"F0.wireOp",EDGE,"E14.0.MirrorCS"),sQuery(id+"F0.wireOp",EDGE,"E15.0.MirrorCS"),sQuery(id+"F0.wireOp",EDGE,"E16.0.MirrorCS"),sQuery(id+"F0.wireOp",EDGE,"E17.0.MirrorCS"),sQuery(id+"F0.wireOp",EDGE,"E18.0.MirrorCS"),sQuery(id+"F0.wireOp",EDGE,"E20.0.MirrorCS"),sQuery(id+"F0.wireOp",EDGE,"E21.0.MirrorCS"),sQuery(id+"F0.wireOp",EDGE,"E22.0.MirrorCS"),sQuery(id+"F0.wireOp",EDGE,"E23.0.MirrorCS"),sQuery(id+"F0.wireOp",EDGE,"E24.0.MirrorCS"),sQuery(id+"F0.wireOp",EDGE,"E25.0.MirrorCS"),sQuery(id+"F0.wireOp",EDGE,"E26.0.MirrorCS"),sQuery(id+"F0.wireOp",EDGE,"E27.0.MirrorCS"),sQuery(id+"F0.wireOp",EDGE,"E28.0.MirrorCS"),sQuery(id+"F0.wireOp",EDGE,"E30.0.MirrorCS"),sQuery(id+"F0.wireOp",EDGE,"E31"),sQuery(id+"F0.wireOp",EDGE,"E32.filletArc"),sQuery(id+"F0.wireOp",EDGE,"E33.filletArc"),sQuery(id+"F0.wireOp",EDGE,"E34.filletArc"),sQuery(id+"F0.wireOp",EDGE,"E35.filletArc"),sQuery(id+"F0.wireOp",EDGE,"E36.filletArc"),sQuery(id+"F0.wireOp",EDGE,"E37.filletArc"),sQuery(id+"F0.wireOp",EDGE,"E38.filletArc"),sQuery(id+"F0.wireOp",EDGE,"E39.filletArc"),sQuery(id+"F0.wireOp",EDGE,"E40.filletArc"),sQuery(id+"F0.wireOp",EDGE,"E41.filletArc"),sQuery(id+"F0.wireOp",EDGE,"E42.filletArc"),sQuery(id+"F0.wireOp",EDGE,"E43.filletArc"),sQuery(id+"F0.wireOp",EDGE,"E44.filletArc"),sQuery(id+"F0.wireOp",EDGE,"E45.filletArc"),sQuery(id+"F0.wireOp",EDGE,"E46.filletArc"),sQuery(id+"F0.wireOp",EDGE,"E47.filletArc"),sQuery(id+"F0.wireOp",EDGE,"E48.filletArc"),sQuery(id+"F0.wireOp",EDGE,"E49.filletArc"),sQuery(id+"F0.wireOp",EDGE,"E50.filletArc"),sQuery(id+"F0.wireOp",EDGE,"E51.filletArc"),sQuery(id+"F0.wireOp",EDGE,"E52.filletArc"),sQuery(id+"F0.wireOp",EDGE,"E53.filletArc"),sQuery(id+"F0.wireOp",EDGE,"E54.filletArc"),sQuery(id+"F0.wireOp",EDGE,"E55.filletArc"),sQuery(id+"F0.wireOp",EDGE,"E56.filletArc"),sQuery(id+"F0.wireOp",EDGE,"E57.filletArc"),sQuery(id+"F0.wireOp",EDGE,"E58.filletArc"),sQuery(id+"F0.wireOp",EDGE,"E59.filletArc")])]}),"instanceName":"2"});
            var Q5;
            Q5=makeQuery(id+"F13.opPattern","COPY",BODY,{"derivedFrom":makeQuery(id+"F3.opExtrude","SWEPT_BODY",BODY,{"disambiguationData":[OSD([sQuery(id+"F2.wireOp",EDGE,"E60.bottom"),sQuery(id+"F2.wireOp",EDGE,"E60.left"),sQuery(id+"F2.wireOp",EDGE,"E61"),sQuery(id+"F2.wireOp",EDGE,"E62")])]}),"instanceName":"1"});
            var Q6;
            Q6=makeQuery(id+"F13.opPattern","COPY",BODY,{"derivedFrom":makeQuery(id+"F1.opExtrude","SWEPT_BODY",BODY,{"disambiguationData":[OSD([sQuery(id+"F0.wireOp",EDGE,"E3"),sQuery(id+"F0.wireOp",EDGE,"E4"),sQuery(id+"F0.wireOp",EDGE,"E5"),sQuery(id+"F0.wireOp",EDGE,"E6"),sQuery(id+"F0.wireOp",EDGE,"E7"),sQuery(id+"F0.wireOp",EDGE,"E8.0.MirrorCS"),sQuery(id+"F0.wireOp",EDGE,"E8.1.MirrorCS"),sQuery(id+"F0.wireOp",EDGE,"E8.2.MirrorCS"),sQuery(id+"F0.wireOp",EDGE,"E8.4.MirrorCS"),sQuery(id+"F0.wireOp",EDGE,"E9.0.MirrorCS"),sQuery(id+"F0.wireOp",EDGE,"E9.1.MirrorCS"),sQuery(id+"F0.wireOp",EDGE,"E9.2.MirrorCS"),sQuery(id+"F0.wireOp",EDGE,"E9.3.MirrorCS"),sQuery(id+"F0.wireOp",EDGE,"E9.4.MirrorCS"),sQuery(id+"F0.wireOp",EDGE,"E9.5.MirrorCS"),sQuery(id+"F0.wireOp",EDGE,"E9.6.MirrorCS"),sQuery(id+"F0.wireOp",EDGE,"E9.7.MirrorCS"),sQuery(id+"F0.wireOp",EDGE,"E9.9.MirrorCS"),sQuery(id+"F0.wireOp",EDGE,"E11.0.MirrorCS"),sQuery(id+"F0.wireOp",EDGE,"E12.0.MirrorCS"),sQuery(id+"F0.wireOp",EDGE,"E13.0.MirrorCS"),sQuery(id+"F0.wireOp",EDGE,"E14.0.MirrorCS"),sQuery(id+"F0.wireOp",EDGE,"E15.0.MirrorCS"),sQuery(id+"F0.wireOp",EDGE,"E16.0.MirrorCS"),sQuery(id+"F0.wireOp",EDGE,"E17.0.MirrorCS"),sQuery(id+"F0.wireOp",EDGE,"E18.0.MirrorCS"),sQuery(id+"F0.wireOp",EDGE,"E20.0.MirrorCS"),sQuery(id+"F0.wireOp",EDGE,"E21.0.MirrorCS"),sQuery(id+"F0.wireOp",EDGE,"E22.0.MirrorCS"),sQuery(id+"F0.wireOp",EDGE,"E23.0.MirrorCS"),sQuery(id+"F0.wireOp",EDGE,"E24.0.MirrorCS"),sQuery(id+"F0.wireOp",EDGE,"E25.0.MirrorCS"),sQuery(id+"F0.wireOp",EDGE,"E26.0.MirrorCS"),sQuery(id+"F0.wireOp",EDGE,"E27.0.MirrorCS"),sQuery(id+"F0.wireOp",EDGE,"E28.0.MirrorCS"),sQuery(id+"F0.wireOp",EDGE,"E30.0.MirrorCS"),sQuery(id+"F0.wireOp",EDGE,"E31"),sQuery(id+"F0.wireOp",EDGE,"E32.filletArc"),sQuery(id+"F0.wireOp",EDGE,"E33.filletArc"),sQuery(id+"F0.wireOp",EDGE,"E34.filletArc"),sQuery(id+"F0.wireOp",EDGE,"E35.filletArc"),sQuery(id+"F0.wireOp",EDGE,"E36.filletArc"),sQuery(id+"F0.wireOp",EDGE,"E37.filletArc"),sQuery(id+"F0.wireOp",EDGE,"E38.filletArc"),sQuery(id+"F0.wireOp",EDGE,"E39.filletArc"),sQuery(id+"F0.wireOp",EDGE,"E40.filletArc"),sQuery(id+"F0.wireOp",EDGE,"E41.filletArc"),sQuery(id+"F0.wireOp",EDGE,"E42.filletArc"),sQuery(id+"F0.wireOp",EDGE,"E43.filletArc"),sQuery(id+"F0.wireOp",EDGE,"E44.filletArc"),sQuery(id+"F0.wireOp",EDGE,"E45.filletArc"),sQuery(id+"F0.wireOp",EDGE,"E46.filletArc"),sQuery(id+"F0.wireOp",EDGE,"E47.filletArc"),sQuery(id+"F0.wireOp",EDGE,"E48.filletArc"),sQuery(id+"F0.wireOp",EDGE,"E49.filletArc"),sQuery(id+"F0.wireOp",EDGE,"E50.filletArc"),sQuery(id+"F0.wireOp",EDGE,"E51.filletArc"),sQuery(id+"F0.wireOp",EDGE,"E52.filletArc"),sQuery(id+"F0.wireOp",EDGE,"E53.filletArc"),sQuery(id+"F0.wireOp",EDGE,"E54.filletArc"),sQuery(id+"F0.wireOp",EDGE,"E55.filletArc"),sQuery(id+"F0.wireOp",EDGE,"E56.filletArc"),sQuery(id+"F0.wireOp",EDGE,"E57.filletArc"),sQuery(id+"F0.wireOp",EDGE,"E58.filletArc"),sQuery(id+"F0.wireOp",EDGE,"E59.filletArc")])]}),"instanceName":"1"});
            var Q7;
            Q7=makeQuery(id+"F3.opExtrude","SWEPT_BODY",BODY,{"disambiguationData":[OSD([sQuery(id+"F2.wireOp",EDGE,"E60.bottom"),sQuery(id+"F2.wireOp",EDGE,"E60.left"),sQuery(id+"F2.wireOp",EDGE,"E61"),sQuery(id+"F2.wireOp",EDGE,"E62")])]});
            var Q8;
            Q8=qCreatedBy(id+"F14.planeOp",FACE);
            mirror(context, id + "F15", {"entities" : qUnion([Q0, Q1, Q2, Q3, Q4, Q5, Q6, Q7]), "mirrorPlane" : qUnion([Q8])});
        }
    });
